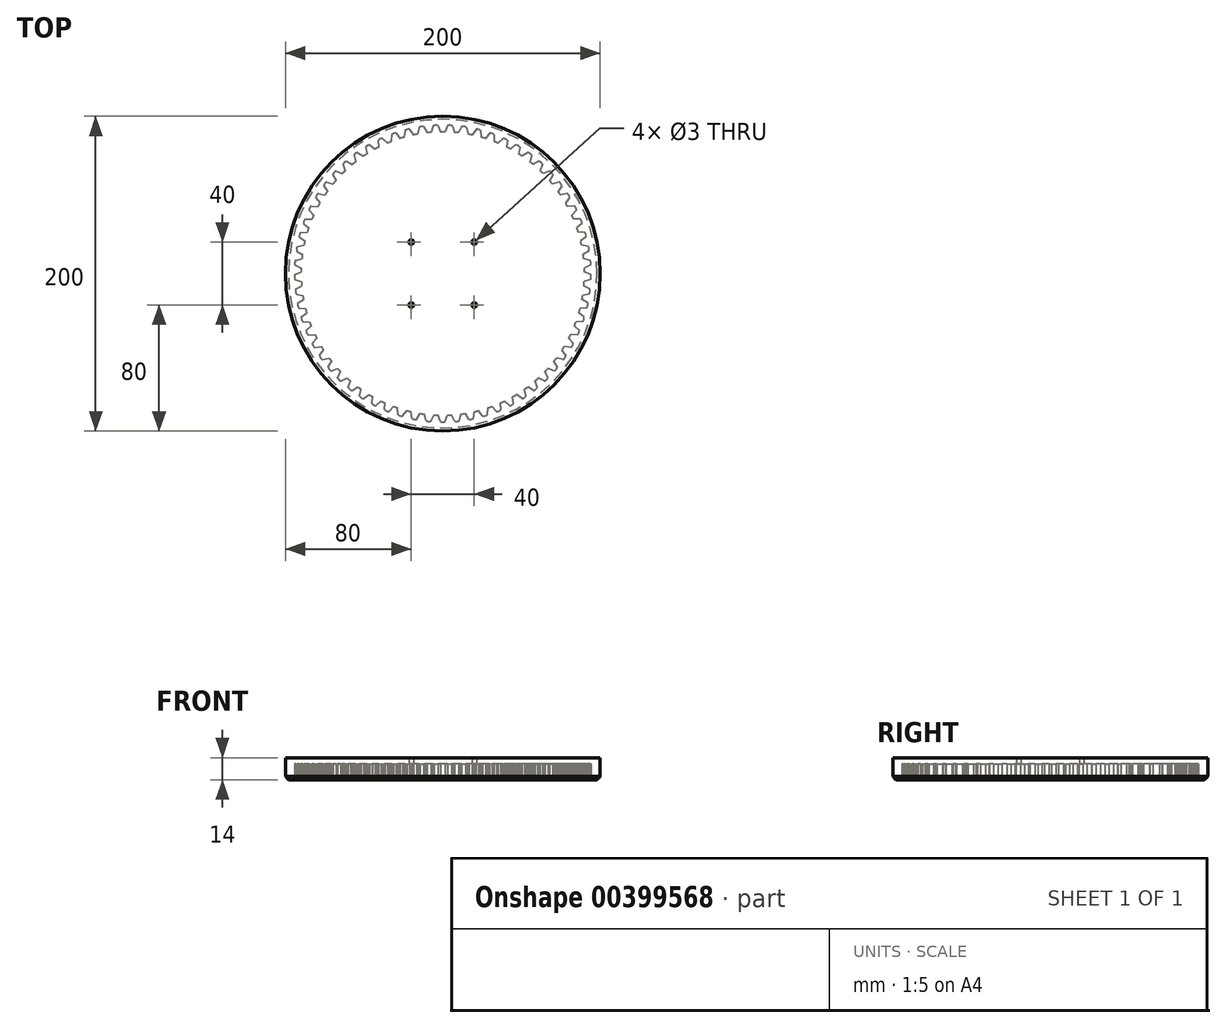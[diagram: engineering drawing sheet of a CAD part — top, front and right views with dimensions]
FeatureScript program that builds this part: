
annotation { "Feature Type Name" : "Feature", "Feature Type Description" : "" }
export const myFeature = defineFeature(function(context is Context, id is Id, definition is map)
    precondition{}
    {
        {
            var Q0;
            Q0=qCreatedBy(makeId("Top.planeOp"),FACE);
            var sketch = newSketch(context, id + "F0", { "sketchPlane" : qUnion([Q0])});
            skCircle(sketch, "E0", {"center": v(0, 0) * mm, "radius": 100 * mm});
            skLineSegment(sketch, "E1", {"start": v(0, -100) * mm, "end": v(0, 0) * mm});
            skLineSegment(sketch, "E2", {"start": v(0, 100) * mm, "end": v(0, 0) * mm});
            skLineSegment(sketch, "E3", {"start": v(0, 0) * mm, "end": v(100, 0) * mm});
            skLineSegment(sketch, "E4", {"start": v(100, 0) * mm, "end": v(0, 0) * mm});
            skLineSegment(sketch, "E5", {"start": v(-100, 0) * mm, "end": v(0, 0) * mm});
            skCircle(sketch, "E6", {"center": v(-20, 20) * mm, "radius": 1.5 * mm});
            skCircle(sketch, "E7", {"center": v(20, 20) * mm, "radius": 1.5 * mm});
            skCircle(sketch, "E8", {"center": v(20, -20) * mm, "radius": 1.5 * mm});
            skCircle(sketch, "E9", {"center": v(-20, -20) * mm, "radius": 1.5 * mm});
            skSolve(sketch);
        }
        {
            var Q0;
            Q0 = qSketchRegion(id + "F0", true);
            extrude(context, id + "F1", {"entities" : qUnion([Q0]), "depth" : 4 * mm});
        }
        {
            var Q0;
            Q0=qCreatedBy(makeId("Top.planeOp"),FACE);
            var sketch = newSketch(context, id + "F2", { "sketchPlane" : qUnion([Q0])});
            skCircle(sketch, "E10", {"center": v(0, 0) * mm, "radius": 90 * mm});
            skCircle(sketch, "E11", {"center": v(0, 0) * mm, "radius": 100 * mm});
            skSolve(sketch);
        }
        {
            var Q0;
            Q0 = qSketchRegion(id + "F2", true);
            extrude(context, id + "F3", {"entities" : qUnion([Q0]), "operationType" : NewBodyOperationType.ADD, "oppositeDirection" : true, "depth" : 10 * mm});
        }
        {
            var Q0;
            Q0=makeQuery(id+"F3.opExtrude","CAP_EDGE",EDGE,{"disambiguationData":[OSD([sQuery(id+"F2.wireOp",EDGE,"E11")])],"isStart":false});
            chamfer(context, id + "F4", {"entities" : qUnion([Q0]), "width" : 2 * mm, "tangentPropagation" : true});
        }
        {
            var Q0;
            Q0=makeQuery(id+"F3.opExtrude","CAP_FACE",FACE,{"disambiguationData":[OSD([sQuery(id+"F2.wireOp",EDGE,"E10"),sQuery(id+"F2.wireOp",EDGE,"E11")])],"isStart":false});
            var sketch = newSketch(context, id + "F5", { "sketchPlane" : qUnion([Q0])});
            skLineSegment(sketch, "E12", {"start": v(0, 0) * mm, "end": v(0, 98) * mm, "construction": true});
            skLineSegment(sketch, "E13", {"start": v(1.53, 93.99) * mm, "end": v(3, 89.95) * mm});
            skLineSegment(sketch, "E14.MirrorCS", {"start": v(-1.53, 93.99) * mm, "end": v(-3, 89.95) * mm});
            skArc(sketch, "E15", {"start": v(3, 89.95) * mm, "mid": v(0, 90) * mm, "end": v(-3, 89.95) * mm});
            skArc(sketch, "E16", {"start": v(1.53, 93.99) * mm, "mid": v(0, 94.28) * mm, "end": v(-1.53, 93.99) * mm});
            skSolve(sketch);
        }
        {
            var Q0;
            Q0 = qSketchRegion(id + "F5", true);
            extrude(context, id + "F6", {"entities" : qUnion([Q0]), "operationType" : NewBodyOperationType.REMOVE, "oppositeDirection" : true, "depth" : 10 * mm});
        }
        {
            var Q0;
            Q0=makeQuery(id+"F6.boolean.opBoolean","COPY",FACE,{"derivedFrom":makeQuery(id+"F6.opExtrude","SWEPT_FACE",FACE,{"disambiguationData":[OSD([sQuery(id+"F5.wireOp",EDGE,"E14.MirrorCS")])]})});
            var Q1;
            Q1=makeQuery(id+"F6.boolean.opBoolean","COPY",FACE,{"derivedFrom":makeQuery(id+"F6.opExtrude","SWEPT_FACE",FACE,{"disambiguationData":[OSD([sQuery(id+"F5.wireOp",EDGE,"E16")])]})});
            var Q2;
            Q2=makeQuery(id+"F6.boolean.opBoolean","COPY",FACE,{"derivedFrom":makeQuery(id+"F6.opExtrude","SWEPT_FACE",FACE,{"disambiguationData":[OSD([sQuery(id+"F5.wireOp",EDGE,"E13")])]})});
            var Q3;
            Q3=makeQuery(id+"F3.opExtrude","SWEPT_FACE",FACE,{"disambiguationData":[OSD([sQuery(id+"F2.wireOp",EDGE,"E10")])]});
            circularPattern(context, id + "F7", {"patternType" : PatternType.FACE, "faces" : qUnion([Q0, Q1, Q2]), "axis" : qUnion([Q3]), "angle" : 360 * degree, "instanceCount" : 65, "equalSpace" : true});
        }
    });
